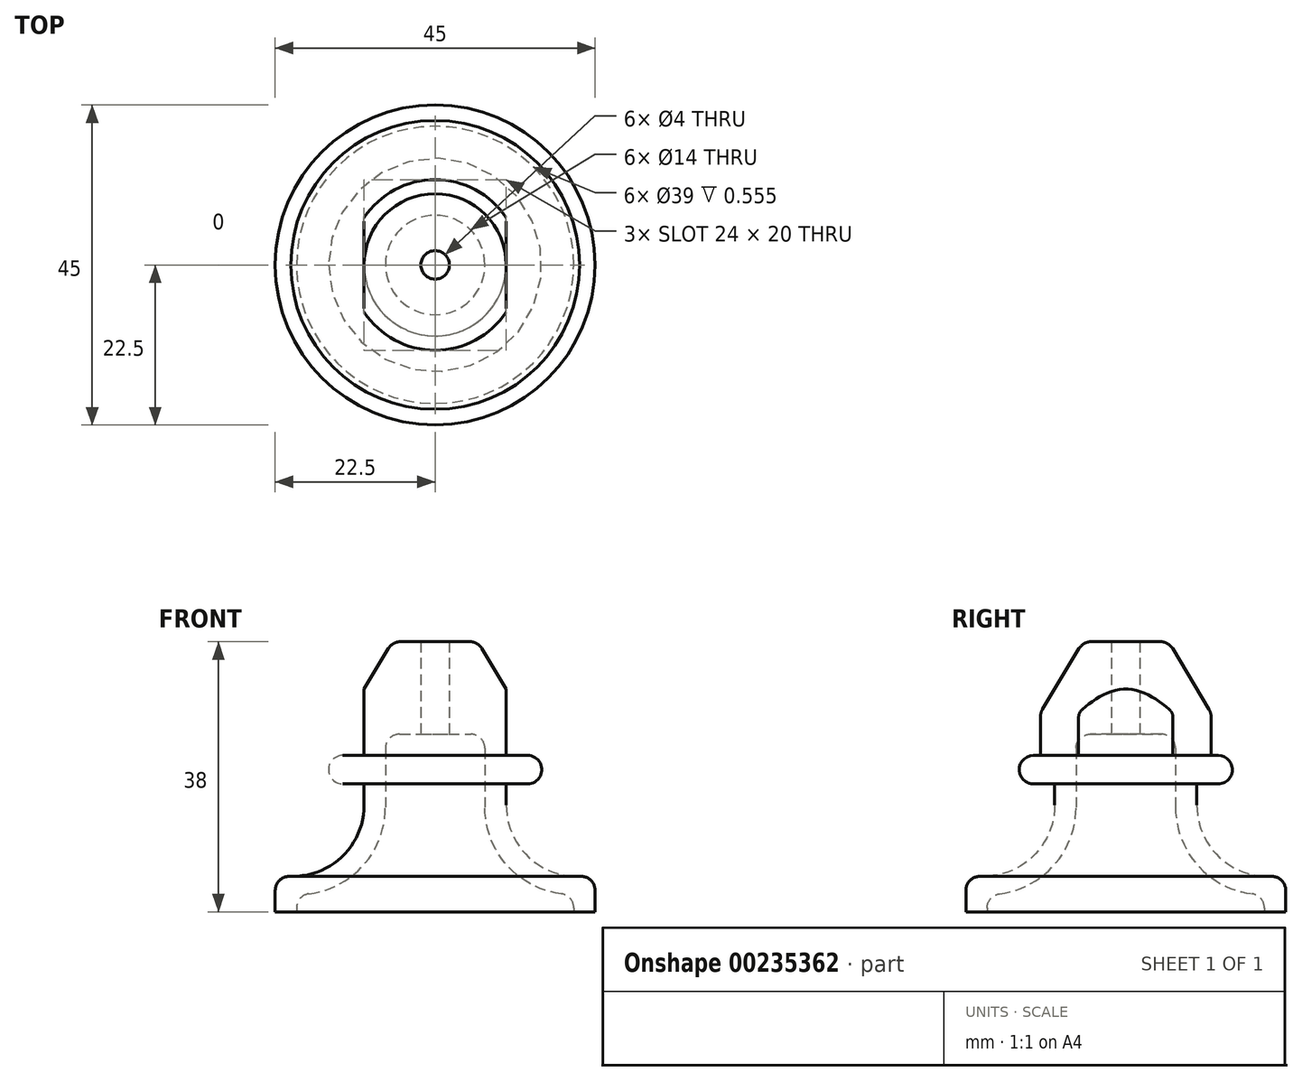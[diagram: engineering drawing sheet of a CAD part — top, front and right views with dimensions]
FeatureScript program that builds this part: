
annotation { "Feature Type Name" : "Feature", "Feature Type Description" : "" }
export const myFeature = defineFeature(function(context is Context, id is Id, definition is map)
    precondition{}
    {
        {
            var Q0;
            Q0=qCreatedBy(makeId("Front.planeOp"),FACE);
            var sketch = newSketch(context, id + "F0", { "sketchPlane" : qUnion([Q0])});
            skLineSegment(sketch, "E0", {"start": v(0, 0) * mm, "end": v(0, 38) * mm});
            skLineSegment(sketch, "E1", {"start": v(0, 38) * mm, "end": v(6, 38) * mm});
            skLineSegment(sketch, "E2", {"start": v(6, 38) * mm, "end": v(12, 28) * mm});
            skLineSegment(sketch, "E3", {"start": v(12, 28) * mm, "end": v(12, 22) * mm});
            skLineSegment(sketch, "E4", {"start": v(12, 22) * mm, "end": v(15, 22) * mm});
            skLineSegment(sketch, "E5", {"start": v(0, 0) * mm, "end": v(22.5, 0) * mm});
            skLineSegment(sketch, "E6", {"start": v(22.5, 0) * mm, "end": v(22.5, 5) * mm});
            skLineSegment(sketch, "E7", {"start": v(22.5, 5) * mm, "end": v(20.3, 5) * mm});
            skLineSegment(sketch, "E8", {"start": v(15, 22) * mm, "end": v(15, 18) * mm});
            skLineSegment(sketch, "E9", {"start": v(15, 18) * mm, "end": v(10, 18) * mm});
            skLineSegment(sketch, "E10", {"start": v(2, 38) * mm, "end": v(2, 25) * mm});
            skLineSegment(sketch, "E11", {"start": v(0, 25) * mm, "end": v(7, 25) * mm});
            skLineSegment(sketch, "E12", {"start": v(7, 25) * mm, "end": v(7, 14.7) * mm});
            skLineSegment(sketch, "E13", {"start": v(19.5, 0) * mm, "end": v(19.5, 2.45) * mm});
            skLineSegment(sketch, "E14", {"start": v(10, 18) * mm, "end": v(10, 18) * mm});
            skArc(sketch, "E15", {"start": v(7, 14.7) * mm, "mid": v(10.68, 5.95) * mm, "end": v(19.5, 2.45) * mm});
            skLineSegment(sketch, "E16", {"start": v(10, 18) * mm, "end": v(10, 15) * mm});
            skArc(sketch, "E17", {"start": v(10, 15) * mm, "mid": v(13.04, 7.82) * mm, "end": v(20.3, 5) * mm});
            skSolve(sketch);
        }
        {
            var Q0;
            {var subQ6=sQuery(id+"F0.wireOp",EDGE,"E2");Q0=makeQuery(id+"F0.imprint","IMPRINT",FACE,{"disambiguationData":[TD([[makeQuery(id+"F0.imprint","IMPRINT",EDGE,{"derivedFrom":subQ6}),-1.0]])]});}
            var Q1;
            Q1=sQuery(id+"F0.wireOp",EDGE,"E0");
            revolve(context, id + "F1", {"entities" : qUnion([Q0]), "axis" : qUnion([Q1]), "revolveType" : RevolveType.FULL});
        }
        {
            var Q0;
            Q0=makeQuery(id+"F1.opRevolve","SWEPT_EDGE",EDGE,{"disambiguationData":[OSD([sQuery(id+"F0.wireOp",EDGE,"E1"),sQuery(id+"F0.wireOp",EDGE,"E2")])]});
            var Q1;
            Q1=makeQuery(id+"F1.opRevolve","SWEPT_EDGE",EDGE,{"disambiguationData":[OSD([sQuery(id+"F0.wireOp",EDGE,"E2"),sQuery(id+"F0.wireOp",EDGE,"E3")])]});
            var Q2;
            Q2=makeQuery(id+"F1.opRevolve","SWEPT_EDGE",EDGE,{"disambiguationData":[OSD([sQuery(id+"F0.wireOp",EDGE,"E4"),sQuery(id+"F0.wireOp",EDGE,"E8")])]});
            var Q3;
            Q3=makeQuery(id+"F1.opRevolve","SWEPT_EDGE",EDGE,{"disambiguationData":[OSD([sQuery(id+"F0.wireOp",EDGE,"E6"),sQuery(id+"F0.wireOp",EDGE,"E7")])]});
            fillet(context, id + "F2", {"entities" : qUnion([Q0, Q1, Q2, Q3]), "radius" : 2 * mm, "tangentPropagation" : true, "allowEdgeOverflow" : false});
        }
        {
            var Q0;
            Q0=makeQuery(id+"F1.opRevolve","SWEPT_EDGE",EDGE,{"disambiguationData":[OSD([sQuery(id+"F0.wireOp",EDGE,"E11"),sQuery(id+"F0.wireOp",EDGE,"E12")])]});
            var Q1;
            Q1=makeQuery(id+"F1.opRevolve","SWEPT_EDGE",EDGE,{"disambiguationData":[OSD([sQuery(id+"F0.wireOp",EDGE,"E13"),sQuery(id+"F0.wireOp",EDGE,"E15")])]});
            fillet(context, id + "F3", {"entities" : qUnion([Q0, Q1]), "radius" : 2 * mm, "tangentPropagation" : true, "allowEdgeOverflow" : false});
        }
        {
            var Q0;
            Q0=makeQuery(id+"F1.opRevolve","SWEPT_FACE",FACE,{"disambiguationData":[OSD([sQuery(id+"F0.wireOp",EDGE,"E1")])]});
            var sketch = newSketch(context, id + "F4", { "sketchPlane" : qUnion([Q0])});
            skCircle(sketch, "E18.0", {"center": v(0, 0) * mm, "radius": 15 * mm, "construction": true});
            skCircle(sketch, "E19", {"center": v(0, 0) * mm, "radius": 15.43 * mm});
            skLineSegment(sketch, "E20.bottom", {"start": v(-10, -11.76) * mm, "end": v(10, -11.76) * mm});
            skLineSegment(sketch, "E20.top", {"start": v(-10, 11.76) * mm, "end": v(10, 11.76) * mm});
            skLineSegment(sketch, "E20.left", {"start": v(-10, -11.76) * mm, "end": v(-10, 11.76) * mm});
            skLineSegment(sketch, "E20.right", {"start": v(10, -11.76) * mm, "end": v(10, 11.76) * mm});
            skSolve(sketch);
        }
        {
            var Q0;
            {var subQ0=sQuery(id+"F4.wireOp",EDGE,"E20.left");Q0=makeQuery(id+"F4.imprint","IMPRINT",FACE,{"disambiguationData":[TD([[makeQuery(id+"F4.imprint","IMPRINT",EDGE,{"derivedFrom":subQ0}),1.0]])]});}
            var Q1;
            {var subQ0=sQuery(id+"F4.wireOp",EDGE,"E20.right");Q1=makeQuery(id+"F4.imprint","IMPRINT",FACE,{"disambiguationData":[TD([[makeQuery(id+"F4.imprint","IMPRINT",EDGE,{"derivedFrom":subQ0}),-1.0]])]});}
            extrude(context, id + "F5", {"entities" : qUnion([Q0, Q1]), "operationType" : NewBodyOperationType.REMOVE, "oppositeDirection" : true, "depth" : 16 * mm});
        }
        {
            var Q0;
            Q0=makeQuery(id+"F1.opRevolve","SWEPT_EDGE",EDGE,{"disambiguationData":[OSD([sQuery(id+"F0.wireOp",EDGE,"E8"),sQuery(id+"F0.wireOp",EDGE,"E9")])]});
            fillet(context, id + "F6", {"entities" : qUnion([Q0]), "radius" : 2 * mm, "tangentPropagation" : true, "allowEdgeOverflow" : false});
        }
    });
